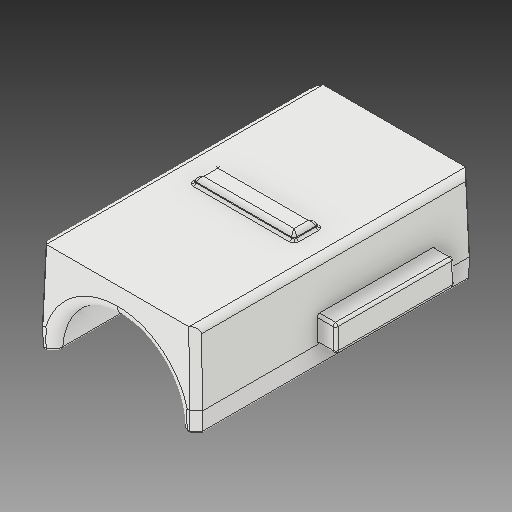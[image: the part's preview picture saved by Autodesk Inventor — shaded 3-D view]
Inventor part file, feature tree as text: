
AUTODESK INVENTOR PART (.ipt)
format: ipt  version: 2019 (Build 230136000, 136)  size: 428,032 bytes
history: native  units: in
note: dims shown in document units (in); Inventor stores cm internally (conversion verified against a paired STEP export)
features: fillet x1
ambient origin geometry x8: Origin, YZ Plane, XZ Plane, XY Plane, X Axis, Y Axis, Z Axis, Center Point
bodies: Solid1 (feature_tree)
feature tree (1):
  fillet  "Fillet17"  [1 undecoded]
note: 1 required parameter value undecoded (feature->parameter linkage not recoverable at this tier; creation-order binding heuristic only, values carry confidence <= 0.55)
